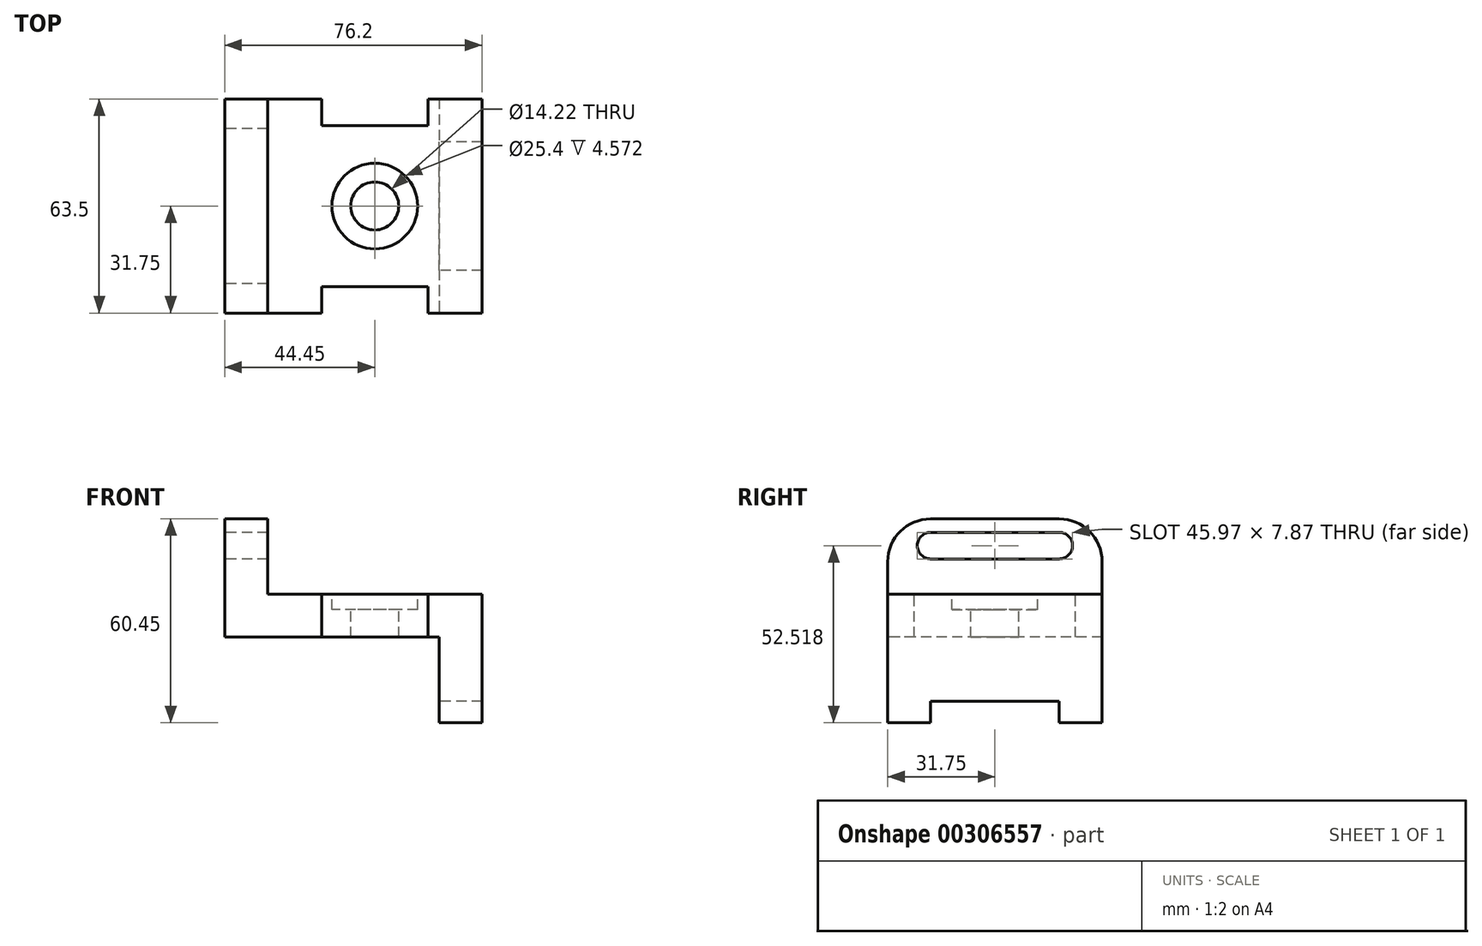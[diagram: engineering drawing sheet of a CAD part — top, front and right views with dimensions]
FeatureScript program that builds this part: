
annotation { "Feature Type Name" : "Feature", "Feature Type Description" : "" }
export const myFeature = defineFeature(function(context is Context, id is Id, definition is map)
    precondition{}
    {
        {
            var Q0;
            Q0=qCreatedBy(makeId("Right.planeOp"),FACE);
            var sketch = newSketch(context, id + "F0", { "sketchPlane" : qUnion([Q0])});
            skLineSegment(sketch, "E0", {"start": v(-31.75, 0) * mm, "end": v(-19.05, 0) * mm});
            skLineSegment(sketch, "E1", {"start": v(-19.05, 0) * mm, "end": v(-19.05, 6.35) * mm});
            skLineSegment(sketch, "E2", {"start": v(-19.05, 6.35) * mm, "end": v(19.05, 6.35) * mm});
            skLineSegment(sketch, "E3", {"start": v(19.05, 6.35) * mm, "end": v(19.05, 0) * mm});
            skLineSegment(sketch, "E4", {"start": v(19.05, 0) * mm, "end": v(31.75, 0) * mm});
            skLineSegment(sketch, "E5", {"start": v(31.75, 0) * mm, "end": v(31.75, 38.1) * mm});
            skLineSegment(sketch, "E6", {"start": v(31.75, 38.1) * mm, "end": v(-31.75, 38.1) * mm});
            skLineSegment(sketch, "E7", {"start": v(-31.75, 38.1) * mm, "end": v(-31.75, 0) * mm});
            skLineSegment(sketch, "E8", {"start": v(-31.75, 38.1) * mm, "end": v(-31.75, 47.75) * mm});
            skLineSegment(sketch, "E9", {"start": v(-19.05, 60.45) * mm, "end": v(19.05, 60.45) * mm});
            skLineSegment(sketch, "E10", {"start": v(31.75, 47.75) * mm, "end": v(31.75, 38.1) * mm});
            skLineSegment(sketch, "E11", {"start": v(-31.75, 52.52) * mm, "end": v(-19.05, 52.52) * mm, "construction": true});
            skLineSegment(sketch, "E12", {"start": v(-19.05, 52.52) * mm, "end": v(19.05, 52.52) * mm, "construction": true});
            skLineSegment(sketch, "E13", {"start": v(19.05, 52.52) * mm, "end": v(31.75, 52.52) * mm, "construction": true});
            skPoint(sketch, "E14.visualSharp", {"position": v(-31.75, 60.45) * mm});
            skArc(sketch, "E14.filletArc", {"start": v(-19.05, 60.45) * mm, "mid": v(-28.03, 56.73) * mm, "end": v(-31.75, 47.75) * mm});
            skCircle(sketch, "E15", {"center": v(-19.05, 52.52) * mm, "radius": 3.94 * mm});
            skCircle(sketch, "E16", {"center": v(19.05, 52.52) * mm, "radius": 3.94 * mm});
            skPoint(sketch, "E17.visualSharp", {"position": v(31.75, 60.45) * mm});
            skArc(sketch, "E17.filletArc", {"start": v(31.75, 47.75) * mm, "mid": v(28.03, 56.73) * mm, "end": v(19.05, 60.45) * mm});
            skLineSegment(sketch, "E18", {"start": v(-19.05, 56.46) * mm, "end": v(19.05, 56.46) * mm});
            skLineSegment(sketch, "E19", {"start": v(-19.05, 48.58) * mm, "end": v(19.05, 48.58) * mm});
            skSolve(sketch);
        }
        {
            var Q0;
            Q0=makeQuery(id+"F0.imprint","IMPRINT",FACE,{"disambiguationData":[TD([[makeQuery(id+"F0.imprint","IMPRINT",EDGE,{"derivedFrom":sQuery(id+"F0.wireOp",EDGE,"E0")}),1.0]])]});
            extrude(context, id + "F1", {"entities" : qUnion([Q0]), "depth" : 76.2 * mm});
        }
        {
            var Q0;
            Q0=makeQuery(id+"F0.imprint","IMPRINT",FACE,{"disambiguationData":[TD([[makeQuery(id+"F0.imprint","IMPRINT",EDGE,{"derivedFrom":sQuery(id+"F0.wireOp",EDGE,"E6")}),-1.0]])]});
            extrude(context, id + "F2", {"entities" : qUnion([Q0]), "operationType" : NewBodyOperationType.ADD, "depth" : 12.7 * mm});
        }
        {
            var Q0;
            Q0=makeQuery(id+"F1.opExtrude","SWEPT_FACE",FACE,{"disambiguationData":[OSD([sQuery(id+"F0.wireOp",EDGE,"E6")])]});
            var sketch = newSketch(context, id + "F3", { "sketchPlane" : qUnion([Q0])});
            skLineSegment(sketch, "E20", {"start": v(12.7, 31.75) * mm, "end": v(28.7, 31.75) * mm});
            skLineSegment(sketch, "E21", {"start": v(28.7, 31.75) * mm, "end": v(28.7, 23.88) * mm});
            skLineSegment(sketch, "E22", {"start": v(28.7, 23.88) * mm, "end": v(60.2, 23.88) * mm});
            skLineSegment(sketch, "E23", {"start": v(60.2, 23.88) * mm, "end": v(60.2, 31.75) * mm});
            skLineSegment(sketch, "E24", {"start": v(60.2, 31.75) * mm, "end": v(76.2, 31.75) * mm});
            skLineSegment(sketch, "E25", {"start": v(12.7, -31.75) * mm, "end": v(28.7, -31.75) * mm});
            skLineSegment(sketch, "E26", {"start": v(28.7, -31.75) * mm, "end": v(28.7, -23.88) * mm});
            skLineSegment(sketch, "E27", {"start": v(28.7, -23.88) * mm, "end": v(60.2, -23.88) * mm});
            skLineSegment(sketch, "E28", {"start": v(60.2, -23.88) * mm, "end": v(60.2, -31.75) * mm});
            skLineSegment(sketch, "E29", {"start": v(60.2, -31.75) * mm, "end": v(76.2, -31.75) * mm});
            skSolve(sketch);
        }
        {
            var Q0;
            {var subQ0=sQuery(id+"F3.wireOp",EDGE,"E21");Q0=makeQuery(id+"F3.imprint","IMPRINT",FACE,{"disambiguationData":[TD([[makeQuery(id+"F3.imprint","IMPRINT",EDGE,{"derivedFrom":subQ0}),1.0]])]});}
            var Q1;
            {var subQ0=sQuery(id+"F3.wireOp",EDGE,"E26");Q1=makeQuery(id+"F3.imprint","IMPRINT",FACE,{"disambiguationData":[TD([[makeQuery(id+"F3.imprint","IMPRINT",EDGE,{"derivedFrom":subQ0}),-1.0]])]});}
            extrude(context, id + "F4", {"entities" : qUnion([Q0, Q1]), "operationType" : NewBodyOperationType.REMOVE, "endBound" : BoundingType.THROUGH_ALL, "oppositeDirection" : true, "depth" : 25.4 * mm});
        }
        {
            var Q0;
            {var subQ1=sQuery(id+"F0.wireOp",EDGE,"E7");Q0=makeQuery(id+"F4.boolean.opBoolean","SPLIT",FACE,{"disambiguationData":[TD([makeQuery(id+"F4.opExtrude","SWEPT_FACE",FACE,{"disambiguationData":[OSD([sQuery(id+"F3.wireOp",EDGE,"E28")])]})])],"derivedFrom":makeQuery(id+"F2.boolean.opBoolean","MERGE",FACE,{"derivedFrom":[makeQuery(id+"F1.opExtrude","SWEPT_FACE",FACE,{"disambiguationData":[OSD([subQ1])]}),makeQuery(id+"F2.opExtrude","SWEPT_FACE",FACE,{"disambiguationData":[OSD([sQuery(id+"F0.wireOp",EDGE,"E8")])]})]})});}
            var sketch = newSketch(context, id + "F5", { "sketchPlane" : qUnion([Q0])});
            skLineSegment(sketch, "E30", {"start": v(76.2, 0) * mm, "end": v(63.5, 0) * mm});
            skLineSegment(sketch, "E31", {"start": v(63.5, 0) * mm, "end": v(63.5, 25.4) * mm});
            skLineSegment(sketch, "E32", {"start": v(63.5, 25.4) * mm, "end": v(62.95, 25.4) * mm});
            skLineSegment(sketch, "E33", {"start": v(62.95, 25.4) * mm, "end": v(60.2, 25.4) * mm});
            skLineSegment(sketch, "E34", {"start": v(60.2, 25.4) * mm, "end": v(60.2, 38.1) * mm});
            skSolve(sketch);
        }
        {
            var Q0;
            {var subQ9=sQuery(id+"F5.wireOp",EDGE,"E31");Q0=makeQuery(id+"F5.imprint","IMPRINT",FACE,{"disambiguationData":[TD([[makeQuery(id+"F5.imprint","IMPRINT",EDGE,{"derivedFrom":subQ9}),1.0]])]});}
            extrude(context, id + "F6", {"entities" : qUnion([Q0]), "operationType" : NewBodyOperationType.REMOVE, "endBound" : BoundingType.THROUGH_ALL, "oppositeDirection" : true, "depth" : 25.4 * mm});
        }
        {
            var Q0;
            Q0=makeQuery(id+"F4.boolean.opBoolean","COPY",FACE,{"derivedFrom":makeQuery(id+"F4.opExtrude","SWEPT_FACE",FACE,{"disambiguationData":[OSD([sQuery(id+"F3.wireOp",EDGE,"E27")])]})});
            var sketch = newSketch(context, id + "F7", { "sketchPlane" : qUnion([Q0])});
            skLineSegment(sketch, "E35", {"start": v(60.2, 25.4) * mm, "end": v(0, 25.4) * mm});
            skLineSegment(sketch, "E36", {"start": v(0, 25.4) * mm, "end": v(0, 0) * mm});
            skLineSegment(sketch, "E37", {"start": v(0, 0) * mm, "end": v(60.2, 0) * mm});
            skLineSegment(sketch, "E38", {"start": v(60.2, 0) * mm, "end": v(60.2, 25.4) * mm});
            skSolve(sketch);
        }
        {
            var Q0;
            {var subQ0=sQuery(id+"F7.wireOp",EDGE,"E38");Q0=makeQuery(id+"F7.imprint","IMPRINT",FACE,{"disambiguationData":[TD([[makeQuery(id+"F7.imprint","IMPRINT",EDGE,{"derivedFrom":subQ0}),1.0]])]});}
            extrude(context, id + "F8", {"entities" : qUnion([Q0]), "operationType" : NewBodyOperationType.REMOVE, "endBound" : BoundingType.THROUGH_ALL, "oppositeDirection" : true, "depth" : 25.4 * mm});
        }
        {
            var Q0;
            {var subQ5=sQuery(id+"F0.wireOp",EDGE,"E14.filletArc");var subQ8=sQuery(id+"F0.wireOp",EDGE,"E8");var subQ10=sQuery(id+"F0.wireOp",EDGE,"E7");Q0=makeQuery(id+"F4.boolean.opBoolean","SPLIT",FACE,{"disambiguationData":[TD([makeQuery(id+"F2.opExtrude","SWEPT_FACE",FACE,{"disambiguationData":[OSD([subQ5])]})])],"derivedFrom":makeQuery(id+"F2.boolean.opBoolean","MERGE",FACE,{"derivedFrom":[makeQuery(id+"F1.opExtrude","SWEPT_FACE",FACE,{"disambiguationData":[OSD([subQ10])]}),makeQuery(id+"F2.opExtrude","SWEPT_FACE",FACE,{"disambiguationData":[OSD([subQ8])]})]})});}
            var sketch = newSketch(context, id + "F9", { "sketchPlane" : qUnion([Q0])});
            skLineSegment(sketch, "E39", {"start": v(28.7, 25.4) * mm, "end": v(0, 25.4) * mm});
            skLineSegment(sketch, "E40", {"start": v(0, 25.4) * mm, "end": v(0, 0) * mm});
            skLineSegment(sketch, "E41", {"start": v(0, 0) * mm, "end": v(28.7, 0) * mm});
            skLineSegment(sketch, "E42", {"start": v(28.7, 0) * mm, "end": v(28.7, 25.4) * mm});
            skSolve(sketch);
        }
        {
            var Q0;
            Q0=makeQuery(id+"F9.imprint","IMPRINT",FACE,{"disambiguationData":[TD([[makeQuery(id+"F9.imprint","IMPRINT",EDGE,{"derivedFrom":sQuery(id+"F9.wireOp",EDGE,"E39")}),1.0]])]});
            extrude(context, id + "F10", {"entities" : qUnion([Q0]), "operationType" : NewBodyOperationType.REMOVE, "endBound" : BoundingType.THROUGH_ALL, "oppositeDirection" : true, "depth" : 25.4 * mm});
        }
        {
            var Q0;
            Q0=makeQuery(id+"F1.opExtrude","SWEPT_FACE",FACE,{"disambiguationData":[OSD([sQuery(id+"F0.wireOp",EDGE,"E6")])]});
            var sketch = newSketch(context, id + "F11", { "sketchPlane" : qUnion([Q0])});
            skLineSegment(sketch, "E43", {"start": v(76.2, 0) * mm, "end": v(44.45, 0) * mm, "construction": true});
            skPoint(sketch, "E43.endSnap0", {"position": v(76.2, 0) * mm});
            skCircle(sketch, "E44", {"center": v(44.45, 0) * mm, "radius": 7.11 * mm});
            skCircle(sketch, "E45", {"center": v(44.45, 0) * mm, "radius": 12.7 * mm});
            skSolve(sketch);
        }
        {
            var Q0;
            Q0=makeQuery(id+"F11.imprint","IMPRINT",FACE,{"disambiguationData":[TD([[makeQuery(id+"F11.imprint","IMPRINT",EDGE,{"derivedFrom":sQuery(id+"F11.wireOp",EDGE,"E44")}),1.0]])]});
            extrude(context, id + "F12", {"entities" : qUnion([Q0]), "operationType" : NewBodyOperationType.REMOVE, "endBound" : BoundingType.THROUGH_ALL, "oppositeDirection" : true, "depth" : 25.4 * mm});
        }
        {
            var Q0;
            Q0=makeQuery(id+"F11.imprint","IMPRINT",FACE,{"disambiguationData":[TD([[makeQuery(id+"F11.imprint","IMPRINT",EDGE,{"derivedFrom":sQuery(id+"F11.wireOp",EDGE,"E44")}),-1.0]])]});
            extrude(context, id + "F13", {"entities" : qUnion([Q0]), "operationType" : NewBodyOperationType.REMOVE, "oppositeDirection" : true, "depth" : 4.57 * mm});
        }
    });
